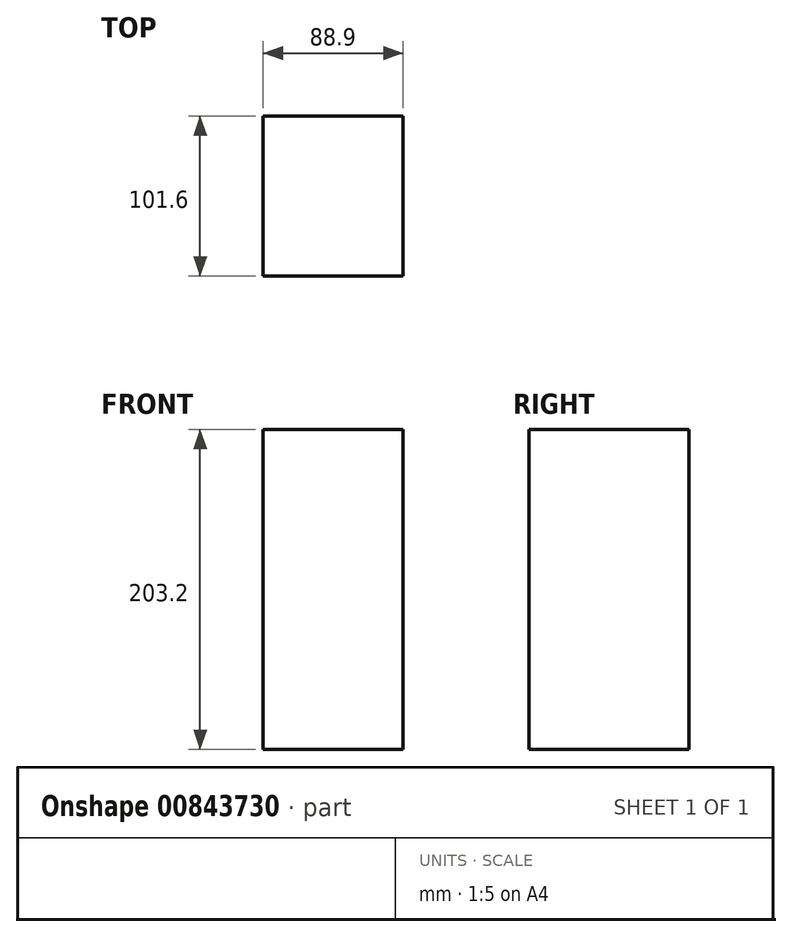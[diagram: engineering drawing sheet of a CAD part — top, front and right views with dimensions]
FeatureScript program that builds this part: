
annotation { "Feature Type Name" : "Feature", "Feature Type Description" : "" }
export const myFeature = defineFeature(function(context is Context, id is Id, definition is map)
    precondition{}
    {
        {
            var Q0;
            Q0=qCreatedBy(makeId("Front.planeOp"),FACE);
            var sketch = newSketch(context, id + "F0", { "sketchPlane" : qUnion([Q0])});
            skLineSegment(sketch, "E0.bottom", {"start": v(0, 0) * mm, "end": v(88.9, 0) * mm});
            skLineSegment(sketch, "E0.top", {"start": v(0, 203.2) * mm, "end": v(88.9, 203.2) * mm});
            skLineSegment(sketch, "E0.left", {"start": v(0, 0) * mm, "end": v(0, 203.2) * mm});
            skLineSegment(sketch, "E0.right", {"start": v(88.9, 0) * mm, "end": v(88.9, 203.2) * mm});
            skSolve(sketch);
        }
        {
            var Q0;
            Q0=makeQuery(id+"F0.imprint","IMPRINT",FACE,{"disambiguationData":[TD([[makeQuery(id+"F0.imprint","IMPRINT",EDGE,{"derivedFrom":sQuery(id+"F0.wireOp",EDGE,"E0.bottom")}),1.0]])]});
            extrude(context, id + "F1", {"entities" : qUnion([Q0]), "depth" : 101.6 * mm, "offsetDistance" : 25.4 * mm});
        }
    });
